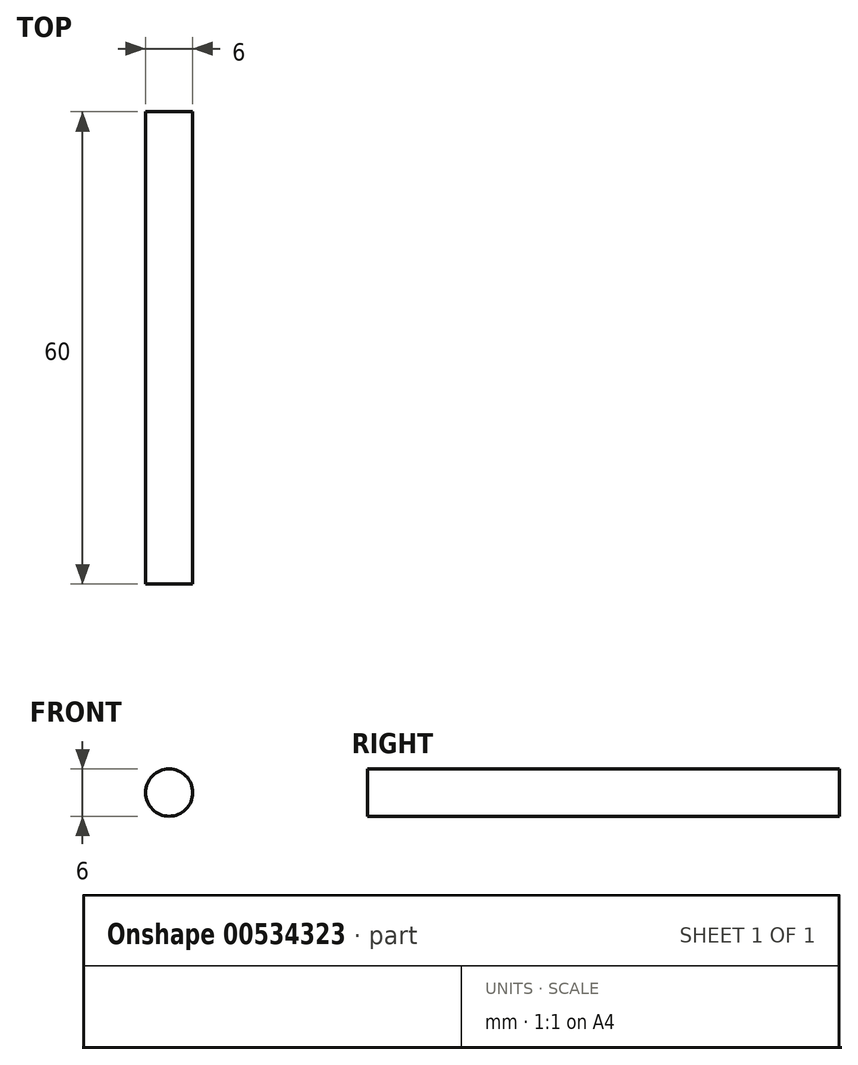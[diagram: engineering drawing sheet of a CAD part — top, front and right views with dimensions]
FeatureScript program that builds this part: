
annotation { "Feature Type Name" : "Feature", "Feature Type Description" : "" }
export const myFeature = defineFeature(function(context is Context, id is Id, definition is map)
    precondition{}
    {
        {
            var Q0;
            Q0=qCreatedBy(makeId("Front.planeOp"),FACE);
            var sketch = newSketch(context, id + "F0", { "sketchPlane" : qUnion([Q0])});
            skCircle(sketch, "E0", {"center": v(0, 0) * mm, "radius": 3 * mm});
            skSolve(sketch);
        }
        {
            var Q0;
            Q0 = qSketchRegion(id + "F0", true);
            extrude(context, id + "F1", {"entities" : qUnion([Q0]), "depth" : 60 * mm, "offsetDistance" : 25 * mm});
        }
    });
